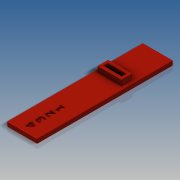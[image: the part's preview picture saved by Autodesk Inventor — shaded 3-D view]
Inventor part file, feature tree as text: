
AUTODESK INVENTOR PART (.ipt)
format: ipt  version: 2016 SP2 (Build 200236200, 236)  size: 271,360 bytes
history: native  units: in
note: dims shown in document units (in); Inventor stores cm internally (conversion verified against a paired STEP export)
features: extrude x4, sketch x1, fillet x1
ambient origin geometry x8: Origin, YZ Plane, XZ Plane, XY Plane, X Axis, Y Axis, Z Axis, Center Point
bodies: Solid1 (feature_tree)
feature tree (6):
  sketch  "Sketch2"  dims[d0=0.315in d1=1.4173in d2=0.0472in d3=0.0in d4=0.252in d5=0.1102in d6=0.0315in d7=0.0315in d8=0.3937in d9=0.0472in d10=0.063in d11=0.0157in d16=0.0268in d18=0.0724in d19=0.0551in d20=0.063in d21=0.0in d22=0.0315in d23=0.0in d24=0.0157in d25=0.0in d26=0.0039in]
  extrude  "Extrusion1"  Depth=0.0039in
  extrude  "Extrusion2"  Depth=0.0472in TaperAngle=0.0deg
  extrude  "Extrusion3"  Depth=0.0039in
  extrude  "Extrusion4"  Depth=0.0039in
  fillet  "Fillet1"  Radius=0.0315in
